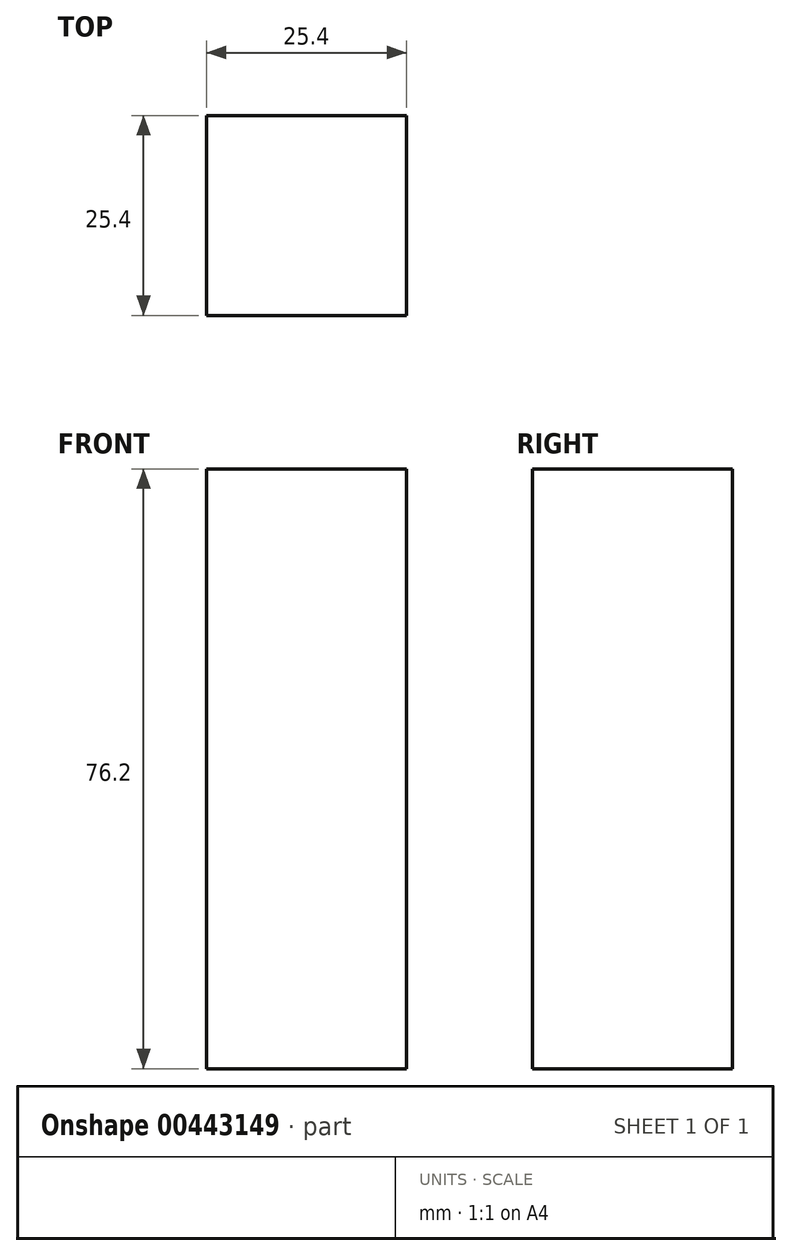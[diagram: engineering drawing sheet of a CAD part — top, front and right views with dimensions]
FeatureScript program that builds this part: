
annotation { "Feature Type Name" : "Feature", "Feature Type Description" : "" }
export const myFeature = defineFeature(function(context is Context, id is Id, definition is map)
    precondition{}
    {
        {
            var Q0;
            Q0=qCreatedBy(makeId("Front.planeOp"),FACE);
            var sketch = newSketch(context, id + "F0", { "sketchPlane" : qUnion([Q0])});
            skLineSegment(sketch, "E0.bottom", {"start": v(-63.02, 66.84) * mm, "end": v(-37.62, 66.84) * mm});
            skLineSegment(sketch, "E0.top", {"start": v(-63.02, -9.36) * mm, "end": v(-37.62, -9.36) * mm});
            skLineSegment(sketch, "E0.left", {"start": v(-63.02, 66.84) * mm, "end": v(-63.02, -9.36) * mm});
            skLineSegment(sketch, "E0.right", {"start": v(-37.62, 66.84) * mm, "end": v(-37.62, -9.36) * mm});
            skSolve(sketch);
        }
        {
            var Q0;
            Q0=makeQuery(id+"F0.imprint","IMPRINT",FACE,{"disambiguationData":[TD([[makeQuery(id+"F0.imprint","IMPRINT",EDGE,{"derivedFrom":sQuery(id+"F0.wireOp",EDGE,"E0.bottom")}),-1.0]])]});
            extrude(context, id + "F1", {"entities" : qUnion([Q0]), "depth" : 25.4 * mm});
        }
    });
